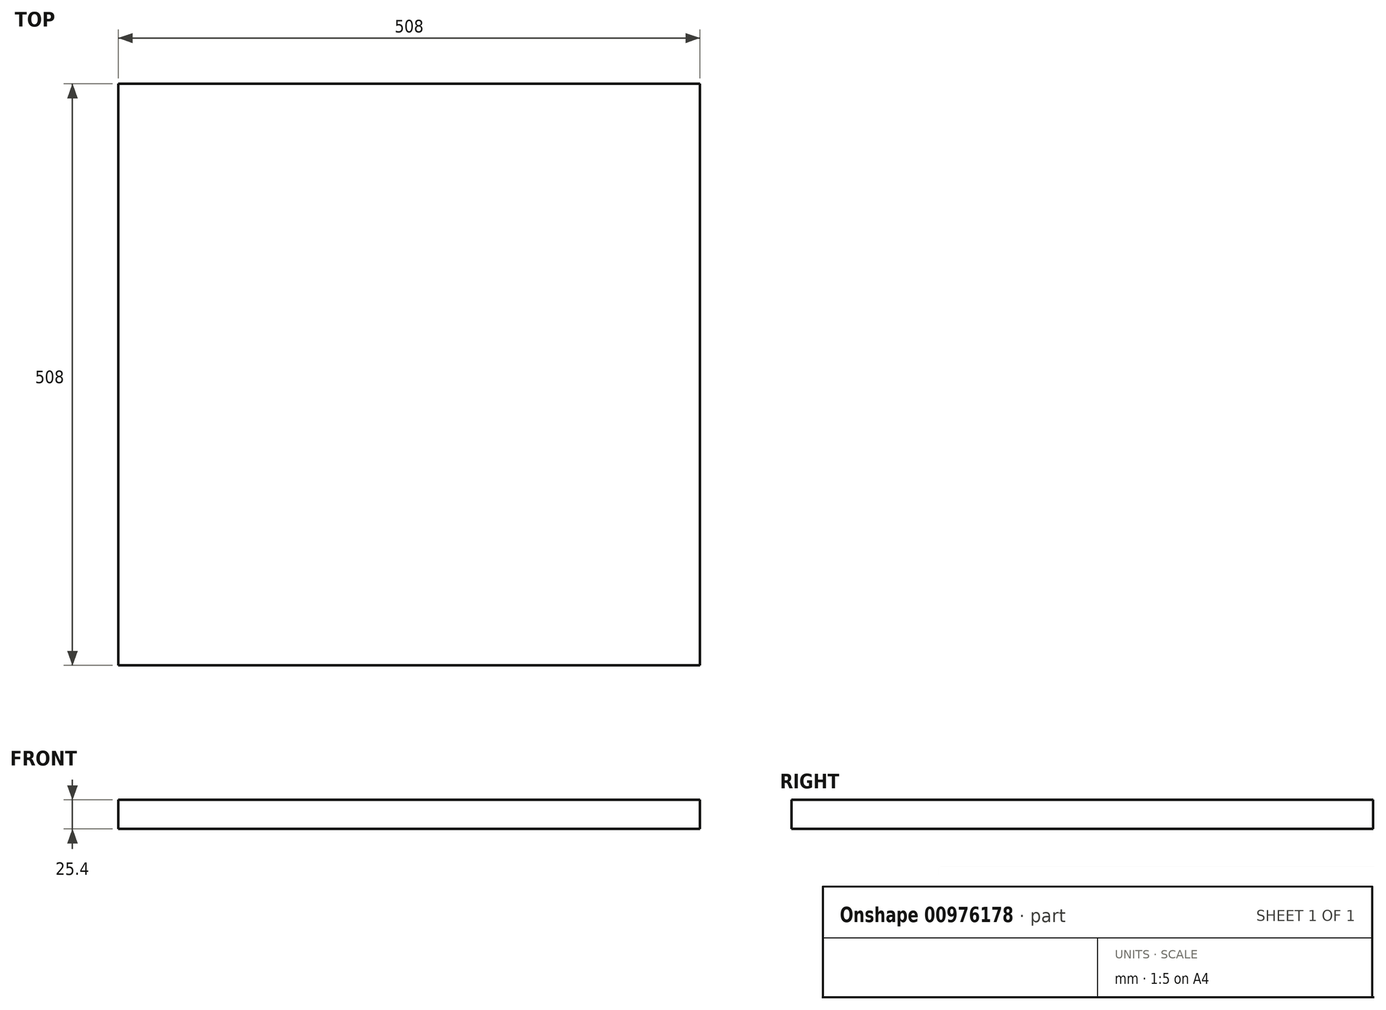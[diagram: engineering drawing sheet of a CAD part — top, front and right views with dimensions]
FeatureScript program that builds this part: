
annotation { "Feature Type Name" : "Feature", "Feature Type Description" : "" }
export const myFeature = defineFeature(function(context is Context, id is Id, definition is map)
    precondition{}
    {
        {
            var Q0;
            Q0=qCreatedBy(makeId("Top.planeOp"),FACE);
            var sketch = newSketch(context, id + "F0", { "sketchPlane" : qUnion([Q0])});
            skLineSegment(sketch, "E0.bottom", {"start": v(-255, 556.16) * mm, "end": v(253, 556.16) * mm});
            skLineSegment(sketch, "E0.top", {"start": v(-255, 48.16) * mm, "end": v(253, 48.16) * mm});
            skLineSegment(sketch, "E0.left", {"start": v(-255, 556.16) * mm, "end": v(-255, 48.16) * mm});
            skLineSegment(sketch, "E0.right", {"start": v(253, 556.16) * mm, "end": v(253, 48.16) * mm});
            skSolve(sketch);
        }
        {
            var Q0;
            Q0=makeQuery(id+"F0.imprint","IMPRINT",FACE,{"disambiguationData":[TD([[makeQuery(id+"F0.imprint","IMPRINT",EDGE,{"derivedFrom":sQuery(id+"F0.wireOp",EDGE,"E0.bottom")}),-1.0]])]});
            var sketch = newSketch(context, id + "F1", { "sketchPlane" : qUnion([Q0])});
            skSolve(sketch);
        }
        {
            var Q0;
            Q0=makeQuery(id+"F1.imprint","IMPRINT",FACE,{"disambiguationData":[TD([[makeQuery(id+"F1.imprint","IMPRINT",EDGE,{"derivedFrom":makeQuery(id+"F0.imprint","IMPRINT",EDGE,{"derivedFrom":sQuery(id+"F0.wireOp",EDGE,"E0.bottom")})}),-1.0]])]});
            extrude(context, id + "F2", {"entities" : qUnion([Q0]), "depth" : 25.4 * mm, "offsetDistance" : 25.4 * mm});
        }
    });
